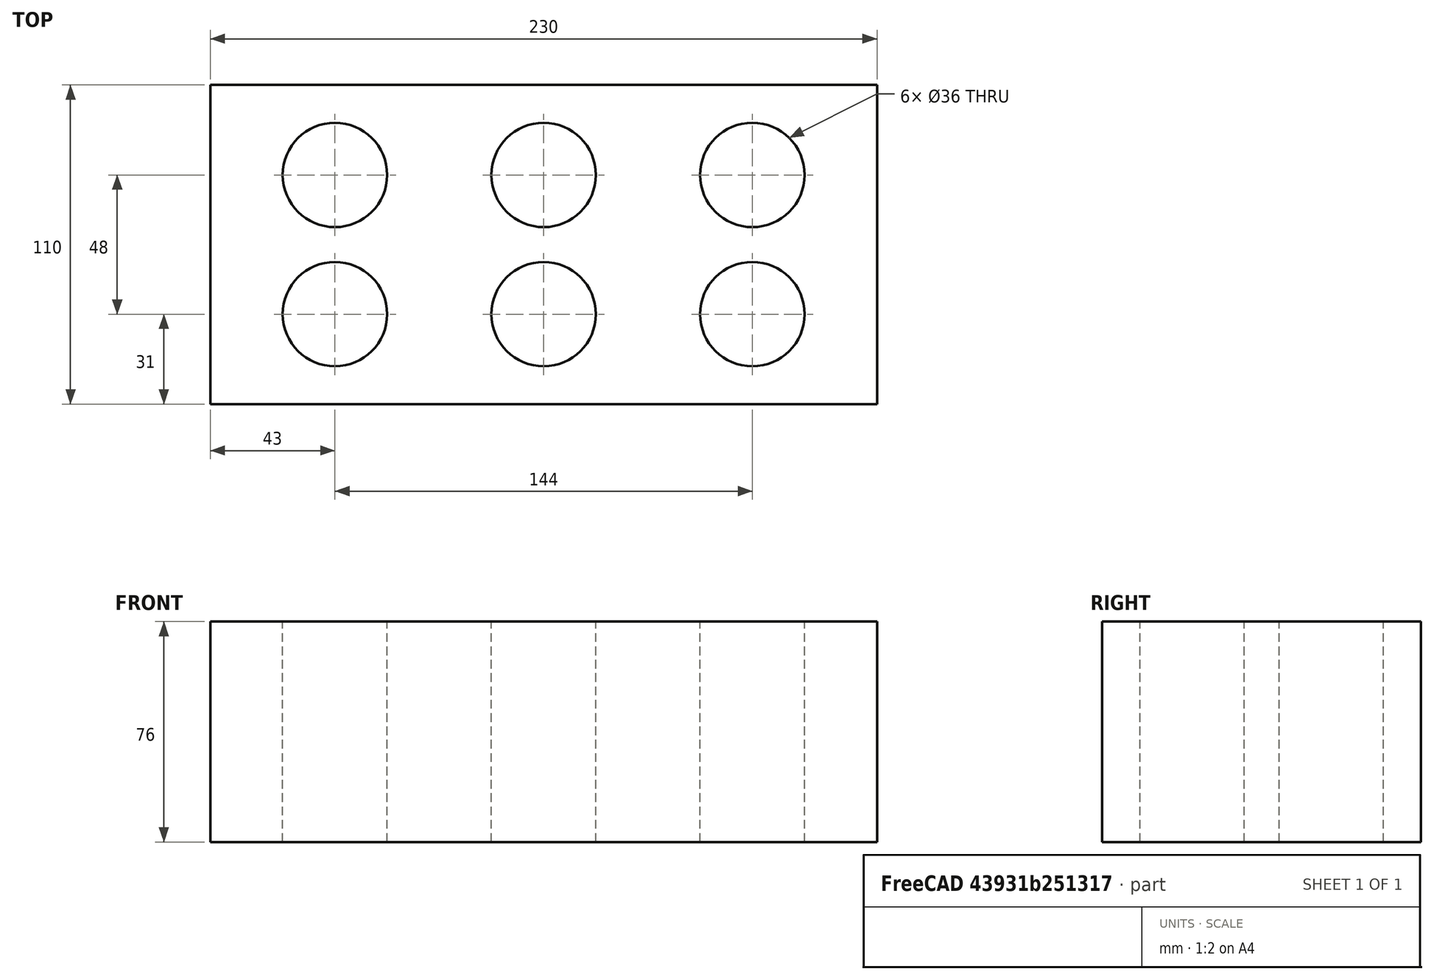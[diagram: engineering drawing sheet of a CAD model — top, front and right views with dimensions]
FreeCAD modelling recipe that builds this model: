
FCSTD DOCUMENT  (FreeCAD 0.18.4R)
Label: tutorial_freecad_ex09_c
License: All rights reserved
LicenseURL: http://en.wikipedia.org/wiki/All_rights_reserved
objects: Part::Cylinder×6, Part::Box×1, Part::MultiFuse×1, Part::Cut×1
note: 9 computed .brp shape members not serialized (recipe doc carries the construction recipe); baked Part::Feature solids carry a one-line shape summary decoded from their .brp

FEATURE [Part::Box] Box  label="base"
  AttacherType = Attacher::AttachEngine3D
  Height = 76
  Length = 230
  Width = 110
FEATURE [Part::Cylinder] Cylinder  label="buraco_001"
  Angle = 360
  AttacherType = Attacher::AttachEngine3D
  Height = 80
  Placement = pos=(0,0,-2) rot=(0,0,1;0rad)
  Radius = 18
FEATURE [Part::Cylinder] Cylinder001  label="buraco_002"
  Angle = 360
  AttacherType = Attacher::AttachEngine3D
  Height = 80
  Placement = pos=(0,48,-2) rot=(0,0,1;0rad)
  Radius = 18
FEATURE [Part::Cylinder] Cylinder002  label="buraco_003"
  Angle = 360
  AttacherType = Attacher::AttachEngine3D
  Height = 80
  Placement = pos=(72,0,-2) rot=(0,0,1;0rad)
  Radius = 18
FEATURE [Part::Cylinder] Cylinder003  label="buraco_004"
  Angle = 360
  AttacherType = Attacher::AttachEngine3D
  Height = 80
  Placement = pos=(72,48,-2) rot=(0,0,1;0rad)
  Radius = 18
FEATURE [Part::Cylinder] Cylinder004  label="buraco_005"
  Angle = 360
  AttacherType = Attacher::AttachEngine3D
  Height = 80
  Placement = pos=(144,0,-2) rot=(0,0,1;0rad)
  Radius = 18
FEATURE [Part::Cylinder] Cylinder005  label="buraco_006"
  Angle = 360
  AttacherType = Attacher::AttachEngine3D
  Height = 80
  Placement = pos=(144,48,-2) rot=(0,0,1;0rad)
  Radius = 18
FEATURE [Part::MultiFuse] Fusion
  Placement = pos=(43,31,0) rot=(0,0,1;0rad)
  Refine = true
  Shapes = -> [Cylinder,Cylinder001,Cylinder003,Cylinder002,Cylinder005,Cylinder004]
FEATURE [Part::Cut] Cut  label="bloque"
  Base = -> Box
  Refine = true
  Tool = -> Fusion
